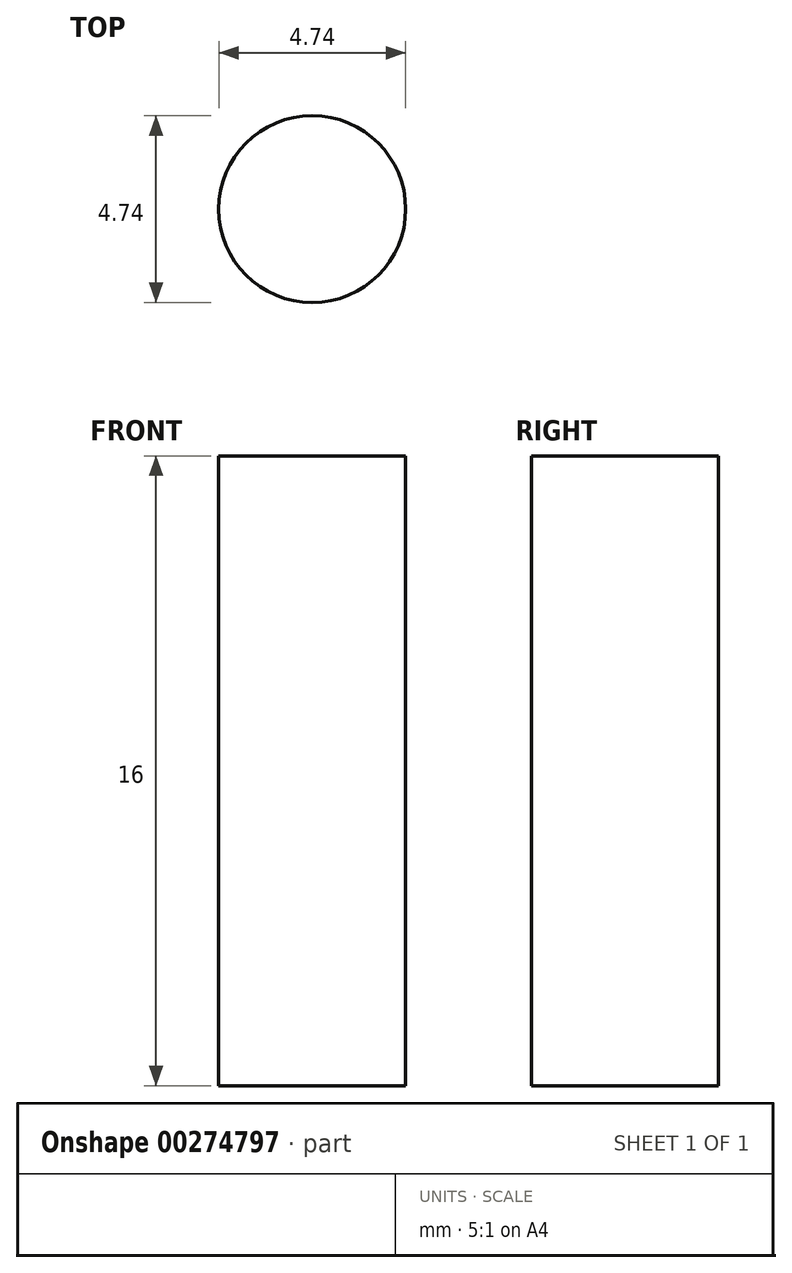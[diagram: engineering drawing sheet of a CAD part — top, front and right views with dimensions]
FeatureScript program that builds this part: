
annotation { "Feature Type Name" : "Feature", "Feature Type Description" : "" }
export const myFeature = defineFeature(function(context is Context, id is Id, definition is map)
    precondition{}
    {
        {
            var Q0;
            Q0=qCreatedBy(makeId("Top.planeOp"),FACE);
            var sketch = newSketch(context, id + "F0", { "sketchPlane" : qUnion([Q0])});
            skCircle(sketch, "E0", {"center": v(0, 0) * mm, "radius": 2.37 * mm});
            skSolve(sketch);
        }
        {
            var Q0;
            Q0 = qSketchRegion(id + "F0", true);
            extrude(context, id + "F1", {"entities" : qUnion([Q0]), "depth" : 16 * mm});
        }
    });
